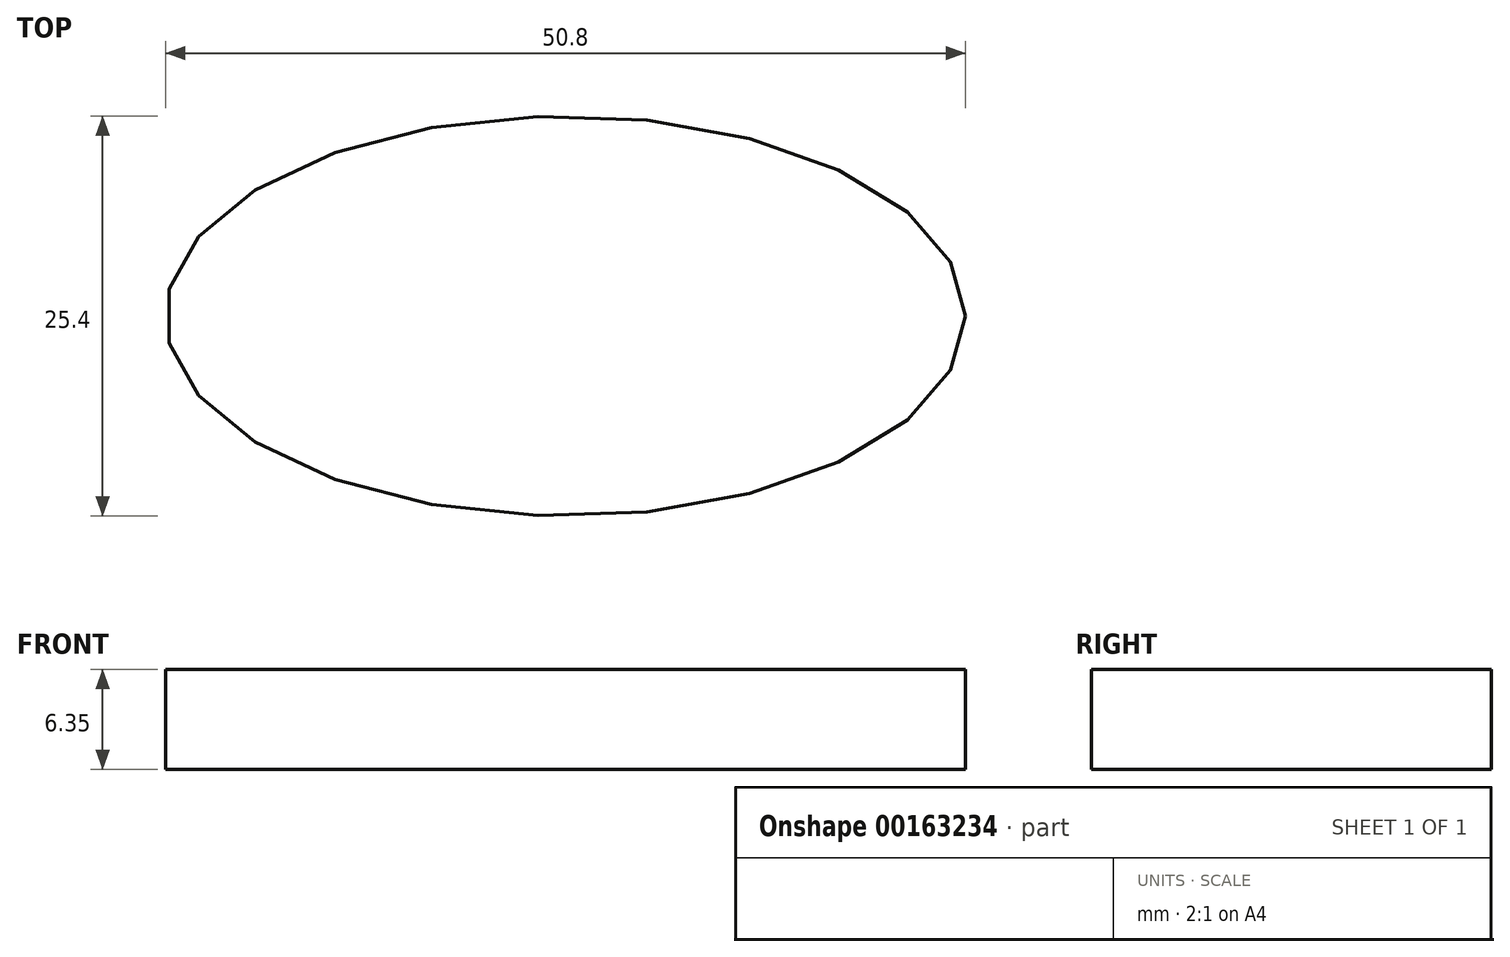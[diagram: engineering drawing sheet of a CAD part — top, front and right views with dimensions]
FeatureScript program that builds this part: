
annotation { "Feature Type Name" : "Feature", "Feature Type Description" : "" }
export const myFeature = defineFeature(function(context is Context, id is Id, definition is map)
    precondition{}
    {
        {
            var Q0;
            Q0=qCreatedBy(makeId("Top.planeOp"),FACE);
            var sketch = newSketch(context, id + "F0", { "sketchPlane" : qUnion([Q0])});
            skEllipse(sketch, "E0", {"center": v(-12.7, 0) * mm, "majorRadius": 25.4 * mm, "minorRadius": 12.7 * mm, "majorAxis": v(1, 0)});
            skSolve(sketch);
        }
        {
            var Q0;
            Q0 = qSketchRegion(id + "F0", true);
            extrude(context, id + "F1", {"entities" : qUnion([Q0]), "depth" : 6.35 * mm});
        }
    });
